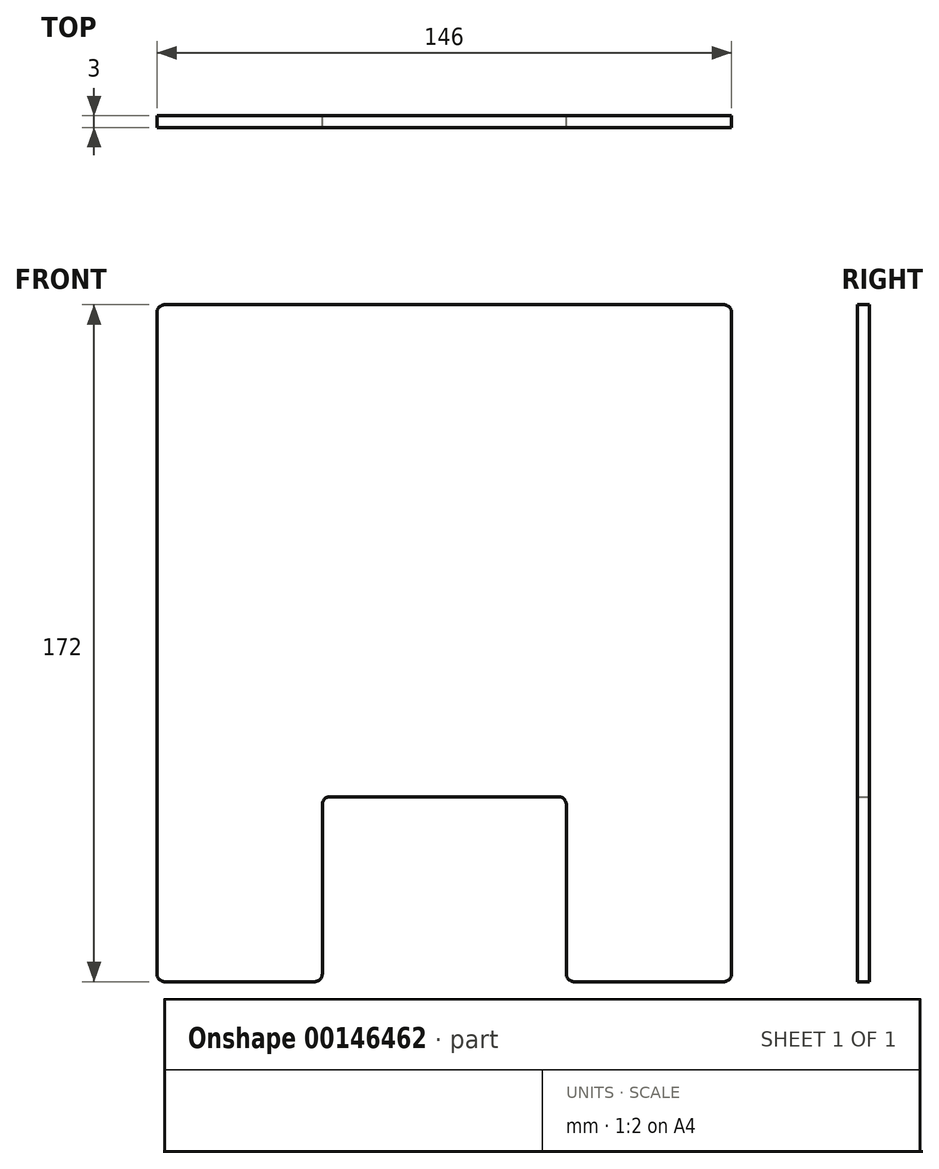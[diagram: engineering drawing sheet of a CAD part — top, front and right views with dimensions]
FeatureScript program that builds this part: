
annotation { "Feature Type Name" : "Feature", "Feature Type Description" : "" }
export const myFeature = defineFeature(function(context is Context, id is Id, definition is map)
    precondition{}
    {
        {
            var Q0;
            Q0=qCreatedBy(makeId("Front.planeOp"),FACE);
            var sketch = newSketch(context, id + "F0", { "sketchPlane" : qUnion([Q0])});
            skLineSegment(sketch, "E0", {"start": v(0, 172) * mm, "end": v(-73, 172) * mm});
            skLineSegment(sketch, "E1", {"start": v(-73, 172) * mm, "end": v(-73, 0) * mm});
            skLineSegment(sketch, "E2", {"start": v(-73, 0) * mm, "end": v(-31, 0) * mm});
            skLineSegment(sketch, "E3", {"start": v(-31, 0) * mm, "end": v(-31, 47) * mm});
            skLineSegment(sketch, "E4", {"start": v(-31, 47) * mm, "end": v(0, 47) * mm});
            skLineSegment(sketch, "E5", {"start": v(0, 47) * mm, "end": v(0, 172) * mm});
            skSolve(sketch);
        }
        {
            var Q0;
            Q0 = qSketchRegion(id + "F0", true);
            extrude(context, id + "F1", {"entities" : qUnion([Q0]), "depth" : 3 * mm, "symmetric" : true});
        }
        {
            var Q0;
            Q0=makeQuery(id+"F1.opExtrude","SWEPT_BODY",BODY,{"disambiguationData":[OSD([sQuery(id+"F0.wireOp",EDGE,"E0"),sQuery(id+"F0.wireOp",EDGE,"E1"),sQuery(id+"F0.wireOp",EDGE,"E2"),sQuery(id+"F0.wireOp",EDGE,"E3"),sQuery(id+"F0.wireOp",EDGE,"E4"),sQuery(id+"F0.wireOp",EDGE,"E5")])]});
            var Q1;
            Q1=qCreatedBy(makeId("Right.planeOp"),FACE);
            mirror(context, id + "F2", {"operationType" : NewBodyOperationType.ADD, "entities" : qUnion([Q0]), "mirrorPlane" : qUnion([Q1])});
        }
        {
            var Q0;
            Q0=makeQuery(id+"F2.opPattern","COPY",EDGE,{"derivedFrom":makeQuery(id+"F1.opExtrude","SWEPT_EDGE",EDGE,{"disambiguationData":[OSD([sQuery(id+"F0.wireOp",EDGE,"E0"),sQuery(id+"F0.wireOp",EDGE,"E1")])]}),"instanceName":"1"});
            var Q1;
            Q1=makeQuery(id+"F1.opExtrude","SWEPT_EDGE",EDGE,{"disambiguationData":[OSD([sQuery(id+"F0.wireOp",EDGE,"E0"),sQuery(id+"F0.wireOp",EDGE,"E1")])]});
            var Q2;
            Q2=makeQuery(id+"F1.opExtrude","SWEPT_EDGE",EDGE,{"disambiguationData":[OSD([sQuery(id+"F0.wireOp",EDGE,"E2"),sQuery(id+"F0.wireOp",EDGE,"E3")])]});
            var Q3;
            Q3=makeQuery(id+"F1.opExtrude","SWEPT_EDGE",EDGE,{"disambiguationData":[OSD([sQuery(id+"F0.wireOp",EDGE,"E1"),sQuery(id+"F0.wireOp",EDGE,"E2")])]});
            var Q4;
            Q4=makeQuery(id+"F1.opExtrude","SWEPT_EDGE",EDGE,{"disambiguationData":[OSD([sQuery(id+"F0.wireOp",EDGE,"E3"),sQuery(id+"F0.wireOp",EDGE,"E4")])]});
            var Q5;
            Q5=makeQuery(id+"F2.opPattern","COPY",EDGE,{"derivedFrom":makeQuery(id+"F1.opExtrude","SWEPT_EDGE",EDGE,{"disambiguationData":[OSD([sQuery(id+"F0.wireOp",EDGE,"E2"),sQuery(id+"F0.wireOp",EDGE,"E3")])]}),"instanceName":"1"});
            var Q6;
            Q6=makeQuery(id+"F2.opPattern","COPY",EDGE,{"derivedFrom":makeQuery(id+"F1.opExtrude","SWEPT_EDGE",EDGE,{"disambiguationData":[OSD([sQuery(id+"F0.wireOp",EDGE,"E3"),sQuery(id+"F0.wireOp",EDGE,"E4")])]}),"instanceName":"1"});
            var Q7;
            Q7=makeQuery(id+"F2.opPattern","COPY",EDGE,{"derivedFrom":makeQuery(id+"F1.opExtrude","SWEPT_EDGE",EDGE,{"disambiguationData":[OSD([sQuery(id+"F0.wireOp",EDGE,"E1"),sQuery(id+"F0.wireOp",EDGE,"E2")])]}),"instanceName":"1"});
            fillet(context, id + "F3", {"entities" : qUnion([Q0, Q1, Q2, Q3, Q4, Q5, Q6, Q7]), "radius" : 2 * mm, "tangentPropagation" : true, "allowEdgeOverflow" : false});
        }
    });
